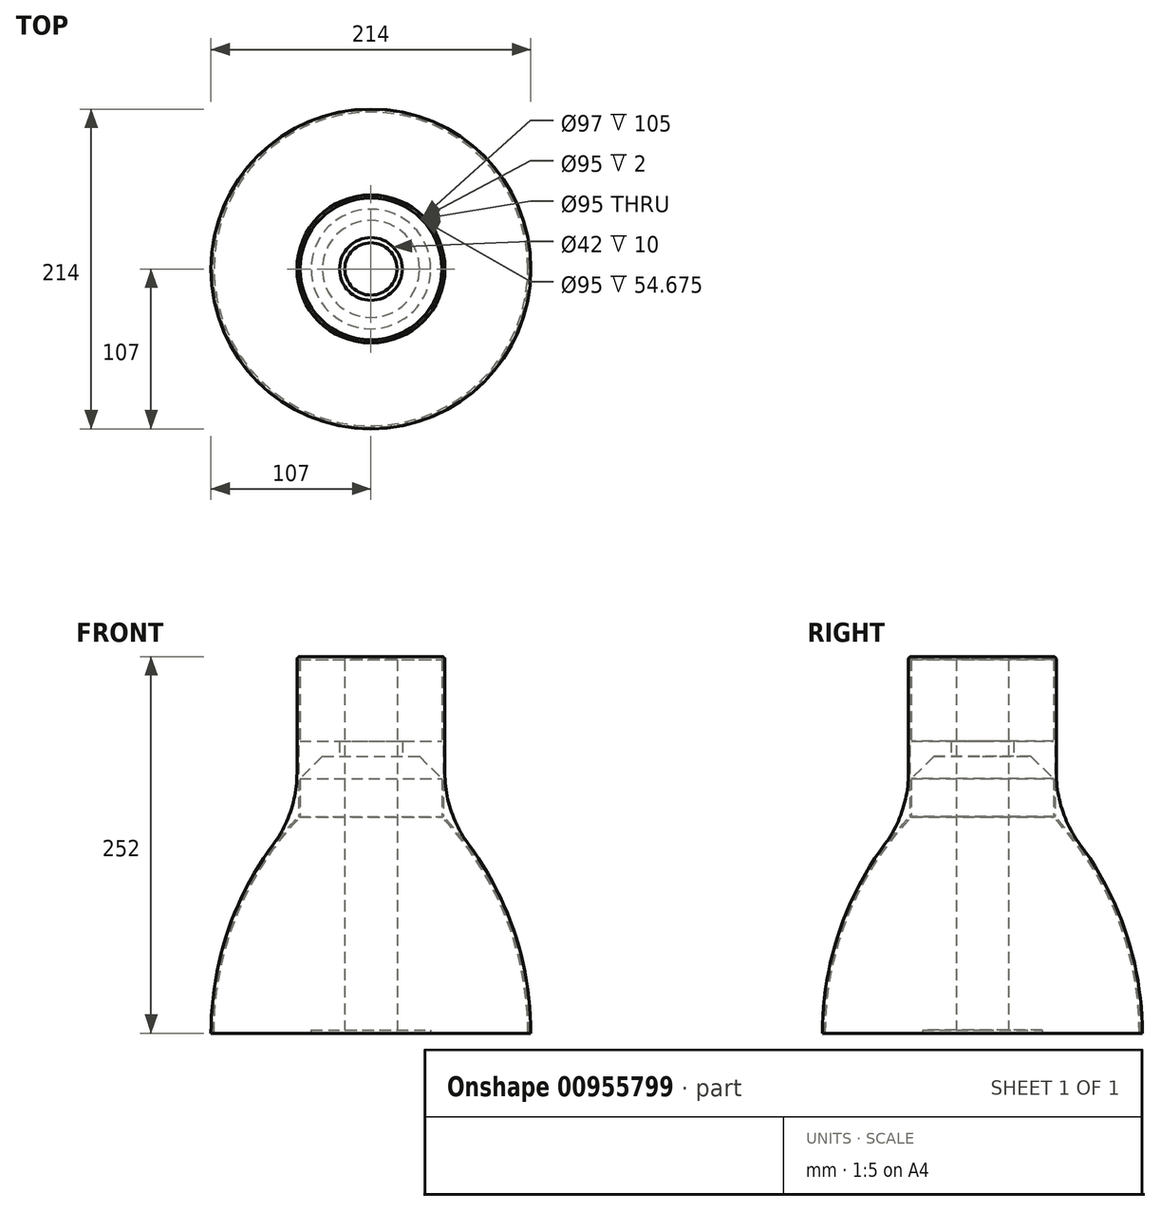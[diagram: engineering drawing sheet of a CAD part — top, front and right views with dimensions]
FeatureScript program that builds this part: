
annotation { "Feature Type Name" : "Feature", "Feature Type Description" : "" }
export const myFeature = defineFeature(function(context is Context, id is Id, definition is map)
    precondition{}
    {
        {
            var Q0;
            Q0=qCreatedBy(makeId("Front.planeOp"),FACE);
            var sketch = newSketch(context, id + "F0", { "sketchPlane" : qUnion([Q0])});
            skLineSegment(sketch, "E0", {"start": v(0, 0) * mm, "end": v(0, 250) * mm, "construction": true});
            skArc(sketch, "E1", {"start": v(-47.5, 144.6) * mm, "mid": v(-90.1, 77.8) * mm, "end": v(-105, 0) * mm});
            skLineSegment(sketch, "E2", {"start": v(-47.5, 144.6) * mm, "end": v(-47.5, 250) * mm});
            skLineSegment(sketch, "E3", {"start": v(-47.5, 190.32) * mm, "end": v(0, 190.32) * mm, "construction": true});
            skCircle(sketch, "E4", {"center": v(0, 90.32) * mm, "radius": 30 * mm, "construction": true});
            skPoint(sketch, "E5", {"position": v(0, 120.32) * mm});
            skLineSegment(sketch, "E6.0", {"start": v(-48.5, 145) * mm, "end": v(-48.5, 250) * mm});
            skArc(sketch, "E6.1", {"start": v(-48.5, 145) * mm, "mid": v(-91.1, 78) * mm, "end": v(-106, 0) * mm});
            skLineSegment(sketch, "E7", {"start": v(-48.5, 250) * mm, "end": v(-47.5, 250) * mm});
            skLineSegment(sketch, "E8", {"start": v(-106, 0) * mm, "end": v(-105, 0) * mm});
            skLineSegment(sketch, "E9.bottom", {"start": v(-47.5, 195.32) * mm, "end": v(0, 195.32) * mm});
            skLineSegment(sketch, "E9.top", {"start": v(-47.5, 185.32) * mm, "end": v(0, 185.32) * mm});
            skLineSegment(sketch, "E9.left", {"start": v(-47.5, 195.32) * mm, "end": v(-47.5, 185.32) * mm});
            skLineSegment(sketch, "E9.right", {"start": v(0, 195.32) * mm, "end": v(0, 185.32) * mm});
            skPoint(sketch, "E9.middle", {"position": v(-23.75, 190.32) * mm});
            skLineSegment(sketch, "E10", {"start": v(-21, 195.32) * mm, "end": v(-21, 185.32) * mm});
            skLineSegment(sketch, "E11", {"start": v(-32.5, 185.32) * mm, "end": v(-47.5, 170.32) * mm});
            skSolve(sketch);
        }
        {
            var Q0;
            {var subQ3=sQuery(id+"F0.wireOp",EDGE,"E1");Q0=makeQuery(id+"F0.imprint","IMPRINT",FACE,{"disambiguationData":[TD([[makeQuery(id+"F0.imprint","IMPRINT",EDGE,{"derivedFrom":subQ3}),-1.0]])]});}
            var Q1;
            {var subQ0=sQuery(id+"F0.wireOp",EDGE,"E11");Q1=makeQuery(id+"F0.imprint","IMPRINT",FACE,{"disambiguationData":[TD([[makeQuery(id+"F0.imprint","IMPRINT",EDGE,{"derivedFrom":subQ0}),-1.0]])]});}
            var Q2;
            {var subQ0=sQuery(id+"F0.wireOp",EDGE,"E10");Q2=makeQuery(id+"F0.imprint","IMPRINT",FACE,{"disambiguationData":[TD([[makeQuery(id+"F0.imprint","IMPRINT",EDGE,{"derivedFrom":subQ0}),-1.0]])]});}
            var Q3;
            Q3=sQuery(id+"F0.wireOp",EDGE,"E0");
            revolve(context, id + "F1", {"surfaceOperationType" : NewSurfaceOperationType.NEW, "entities" : qUnion([Q0, Q1, Q2]), "axis" : qUnion([Q3]), "revolveType" : RevolveType.FULL});
        }
        {
            var Q0;
            Q0=qCreatedBy(makeId("Front.planeOp"),FACE);
            var sketch = newSketch(context, id + "F2", { "sketchPlane" : qUnion([Q0])});
            skLineSegment(sketch, "E12.0", {"start": v(-48.5, 145) * mm, "end": v(-48.5, 250) * mm});
            skArc(sketch, "E12.1", {"start": v(-48.5, 145) * mm, "mid": v(-91.1, 78) * mm, "end": v(-106, 0) * mm});
            skLineSegment(sketch, "E13.0", {"start": v(-49.5, 145.4) * mm, "end": v(-49.5, 250) * mm});
            skArc(sketch, "E13.1", {"start": v(-49.5, 145.4) * mm, "mid": v(-92.1, 78.18) * mm, "end": v(-107, 0) * mm});
            skLineSegment(sketch, "E14", {"start": v(-107, 0) * mm, "end": v(-106, 0) * mm});
            skArc(sketch, "E15", {"start": v(-47.5, 252) * mm, "mid": v(-48.91, 251.41) * mm, "end": v(-49.5, 250) * mm});
            skLineSegment(sketch, "E16", {"start": v(-47.5, 252) * mm, "end": v(-47.5, 250) * mm});
            skLineSegment(sketch, "E17", {"start": v(-48.5, 250) * mm, "end": v(-47.5, 250) * mm});
            skSolve(sketch);
        }
        {
            var Q0;
            Q0 = qSketchRegion(id + "F2", true);
            var Q1;
            Q1=sQuery(id+"F0.wireOp",EDGE,"E0");
            revolve(context, id + "F3", {"surfaceOperationType" : NewSurfaceOperationType.NEW, "entities" : qUnion([Q0]), "axis" : qUnion([Q1]), "revolveType" : RevolveType.FULL});
        }
        {
            var Q0;
            Q0=makeQuery(id+"F3.opRevolve","SWEPT_FACE",FACE,{"disambiguationData":[OSD([sQuery(id+"F2.wireOp",EDGE,"E14")])]});
            var sketch = newSketch(context, id + "F4", { "sketchPlane" : qUnion([Q0])});
            skCircle(sketch, "E18", {"center": v(0, 0) * mm, "radius": 17.5 * mm});
            skCircle(sketch, "E19", {"center": v(0, 0) * mm, "radius": 40 * mm});
            skLineSegment(sketch, "E20", {"start": v(0, 40) * mm, "end": v(0, -40) * mm});
            skSolve(sketch);
        }
        {
            var Q0;
            {var subQ0=sQuery(id+"F4.wireOp",EDGE,"E20");var subQ1=sQuery(id+"F4.wireOp",EDGE,"E18");var subQ2=makeQuery(id+"F4.imprint","INTERSECT",VERTEX,{"disambiguationData":[OD(0.0)],"derivedFrom":[subQ1,subQ0]});Q0=makeQuery(id+"F4.imprint","IMPRINT",FACE,{"disambiguationData":[TD([[makeQuery(id+"F4.imprint","IMPRINT",EDGE,{"disambiguationData":[TD([[subQ2,-1.0]])],"derivedFrom":subQ1}),1.0]])]});}
            var Q1;
            Q1=makeQuery(id+"F1.opRevolve","SWEPT_FACE",FACE,{"disambiguationData":[OSD([sQuery(id+"F0.wireOp",EDGE,"E7")])]});
            extrude(context, id + "F5", {"entities" : qUnion([Q0]), "endBound" : BoundingType.UP_TO_SURFACE, "oppositeDirection" : true, "depth" : 25 * mm, "endBoundEntityFace" : qUnion([Q1]), "offsetDistance" : 25 * mm});
        }
        {
            var Q0;
            {var subQ0=sQuery(id+"F4.wireOp",EDGE,"E20");var subQ1=sQuery(id+"F4.wireOp",EDGE,"E18");var subQ2=makeQuery(id+"F4.imprint","INTERSECT",VERTEX,{"disambiguationData":[OD(0.0)],"derivedFrom":[subQ1,subQ0]});Q0=makeQuery(id+"F4.imprint","IMPRINT",FACE,{"disambiguationData":[TD([[makeQuery(id+"F4.imprint","IMPRINT",EDGE,{"disambiguationData":[TD([[subQ2,-1.0]])],"derivedFrom":subQ1}),-1.0]])]});}
            extrude(context, id + "F6", {"entities" : qUnion([Q0]), "operationType" : NewBodyOperationType.ADD, "oppositeDirection" : true, "depth" : 2 * mm, "offsetDistance" : 25 * mm});
        }
        {
            var Q0;
            {var subQ0=sQuery(id+"F4.wireOp",EDGE,"E20");var subQ1=sQuery(id+"F4.wireOp",EDGE,"E18");var subQ2=makeQuery(id+"F4.imprint","INTERSECT",VERTEX,{"disambiguationData":[OD(0.0)],"derivedFrom":[subQ1,subQ0]});Q0=makeQuery(id+"F4.imprint","IMPRINT",FACE,{"disambiguationData":[TD([[makeQuery(id+"F4.imprint","IMPRINT",EDGE,{"disambiguationData":[TD([[subQ2,1.0]])],"derivedFrom":subQ1}),1.0]])]});}
            var Q1;
            Q1=makeQuery(id+"F5.opExtrude","CAP_FACE",FACE,{"disambiguationData":[OSD([sQuery(id+"F4.wireOp",EDGE,"E18"),sQuery(id+"F4.wireOp",EDGE,"E20")])],"isStart":false});
            extrude(context, id + "F7", {"entities" : qUnion([Q0]), "endBound" : BoundingType.UP_TO_SURFACE, "oppositeDirection" : true, "depth" : 25 * mm, "endBoundEntityFace" : qUnion([Q1]), "offsetDistance" : 25 * mm});
        }
        {
            var Q0;
            {var subQ0=sQuery(id+"F4.wireOp",EDGE,"E20");var subQ1=sQuery(id+"F4.wireOp",EDGE,"E18");var subQ2=makeQuery(id+"F4.imprint","INTERSECT",VERTEX,{"disambiguationData":[OD(0.0)],"derivedFrom":[subQ1,subQ0]});Q0=makeQuery(id+"F4.imprint","IMPRINT",FACE,{"disambiguationData":[TD([[makeQuery(id+"F4.imprint","IMPRINT",EDGE,{"disambiguationData":[TD([[subQ2,1.0]])],"derivedFrom":subQ1}),-1.0]])]});}
            extrude(context, id + "F8", {"entities" : qUnion([Q0]), "operationType" : NewBodyOperationType.ADD, "oppositeDirection" : true, "depth" : 2 * mm, "offsetDistance" : 25 * mm});
        }
        {
            var Q0;
            Q0=makeQuery(id+"F3.opRevolve","SWEPT_EDGE",EDGE,{"disambiguationData":[OSD([sQuery(id+"F2.wireOp",EDGE,"E13.0"),sQuery(id+"F2.wireOp",EDGE,"E13.1")])]});
            fillet(context, id + "F9", {"entities" : qUnion([Q0]), "radius" : 80 * mm, "tangentPropagation" : true, "allowEdgeOverflow" : false});
        }
    });
